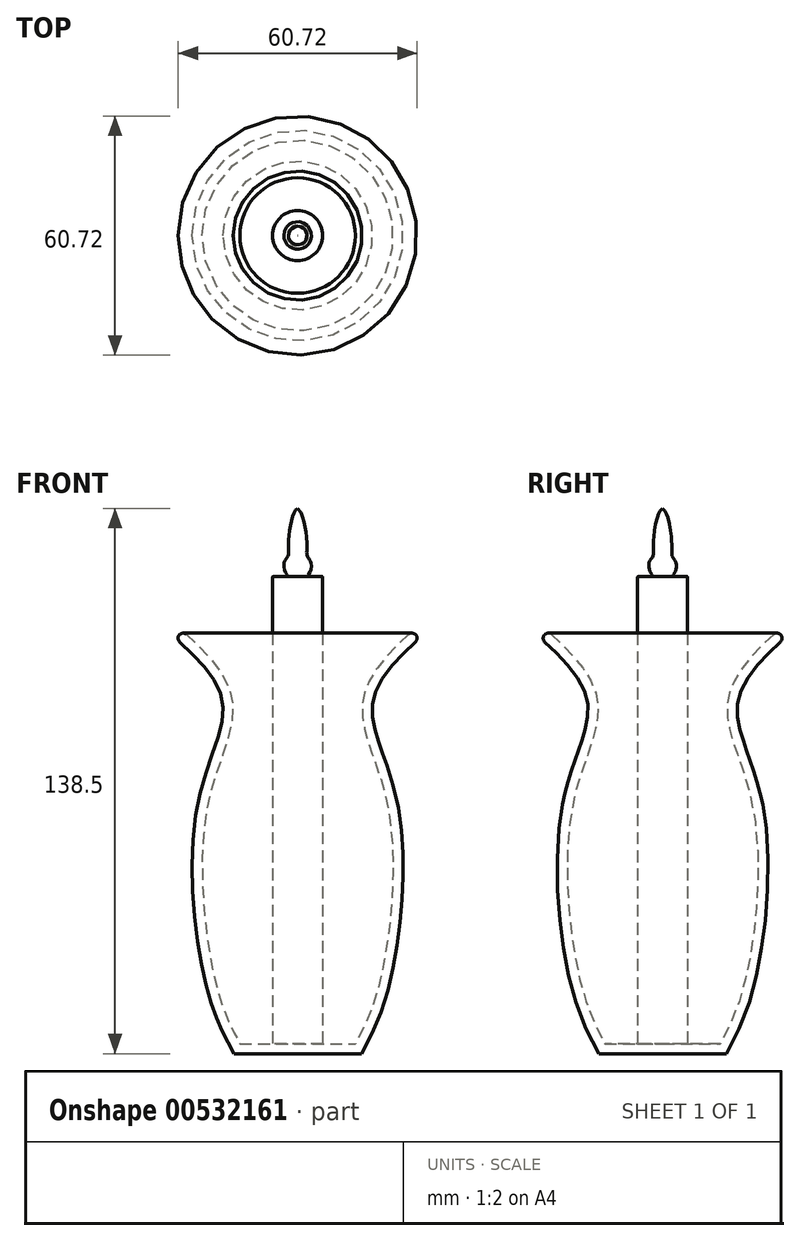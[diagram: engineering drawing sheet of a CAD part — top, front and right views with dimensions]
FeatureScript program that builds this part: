
annotation { "Feature Type Name" : "Feature", "Feature Type Description" : "" }
export const myFeature = defineFeature(function(context is Context, id is Id, definition is map)
    precondition{}
    {
        {
            var Q0;
            Q0=qCreatedBy(makeId("Front.planeOp"),FACE);
            var sketch = newSketch(context, id + "F0", { "sketchPlane" : qUnion([Q0])});
            skLineSegment(sketch, "E0", {"start": v(0, 51.45) * mm, "end": v(-32.36, 51.45) * mm});
            skPoint(sketch, "E1.4.internal.snap0", {"position": v(-16.18, 51.45) * mm});
            skFitSpline(sketch, "E1", {"points": [v(-32.36, 51.45) * mm, v(-19.09, 34.02) * mm, v(-25.3, 8.5) * mm, v(-23.03, -39) * mm, v(-16.18, -55.4) * mm], "startDerivative": vector(82.3, -74.73) * mm, "endDerivative": vector(36.18, -66.1) * mm});
            skLineSegment(sketch, "E2", {"start": v(-16.18, -55.4) * mm, "end": v(0, -55.4) * mm});
            skLineSegment(sketch, "E3", {"start": v(0, -55.4) * mm, "end": v(0, 51.45) * mm});
            skSolve(sketch);
        }
        {
            var Q0;
            Q0=makeQuery(id+"F0.imprint","IMPRINT",FACE,{"disambiguationData":[TD([[makeQuery(id+"F0.imprint","IMPRINT",EDGE,{"derivedFrom":sQuery(id+"F0.wireOp",EDGE,"E0")}),1.0]])]});
            var Q1;
            Q1=sQuery(id+"F0.wireOp",EDGE,"E3");
            revolve(context, id + "F1", {"entities" : qUnion([Q0]), "axis" : qUnion([Q1]), "revolveType" : RevolveType.FULL});
        }
        {
            var Q0;
            Q0=makeQuery(id+"F1.opRevolve","SWEPT_FACE",FACE,{"disambiguationData":[OSD([sQuery(id+"F0.wireOp",EDGE,"E0")])]});
            shell(context, id + "F2", {"entities" : qUnion([Q0]), "thickness" : 2.54 * mm});
        }
        {
            var Q0;
            Q0=makeQuery(id+"F2.opShell","OFFSET_FACE",FACE,{"disambiguationData":[OSD([sQuery(id+"F0.wireOp",EDGE,"E2")])]});
            var sketch = newSketch(context, id + "F3", { "sketchPlane" : qUnion([Q0])});
            skCircle(sketch, "E4", {"center": v(0, 0) * mm, "radius": 6.35 * mm});
            skSolve(sketch);
        }
        {
            var Q0;
            Q0 = qSketchRegion(id + "F3", true);
            extrude(context, id + "F4", {"entities" : qUnion([Q0]), "operationType" : NewBodyOperationType.ADD, "depth" : 118.76 * mm, "offsetDistance" : 25.4 * mm});
        }
        {
            var Q0;
            Q0=qCreatedBy(makeId("Front.planeOp"),FACE);
            var sketch = newSketch(context, id + "F5", { "sketchPlane" : qUnion([Q0])});
            skFitSpline(sketch, "E5", {"points": [v(0, 83.11) * mm, v(-2.34, 73.84) * mm, v(-2.5, 70.87) * mm, v(-3.47, 69.15) * mm, v(-2.29, 65.9) * mm, v(0, 65.92) * mm], "startDerivative": vector(-14.49, -6.91) * mm, "endDerivative": vector(13.28, 4.08) * mm});
            skLineSegment(sketch, "E6", {"start": v(0, 83.11) * mm, "end": v(0, 65.92) * mm});
            skSolve(sketch);
        }
        {
            var Q0;
            Q0=makeQuery(id+"F5.imprint","IMPRINT",FACE,{"disambiguationData":[TD([[makeQuery(id+"F5.imprint","IMPRINT",EDGE,{"derivedFrom":sQuery(id+"F5.wireOp",EDGE,"E5")}),1.0]])]});
            var Q1;
            Q1=sQuery(id+"F5.wireOp",EDGE,"E6");
            revolve(context, id + "F6", {"operationType" : NewBodyOperationType.ADD, "entities" : qUnion([Q0]), "axis" : qUnion([Q1]), "revolveType" : RevolveType.FULL});
        }
        {
            var Q0;
            {var subQ0=sQuery(id+"F3.wireOp",EDGE,"E4");Q0=makeQuery(id+"F6.boolean.opBoolean","SPLIT",FACE,{"disambiguationData":[TD([makeQuery(id+"F4.opExtrude","SWEPT_FACE",FACE,{"disambiguationData":[OSD([subQ0])]}),makeQuery(id+"F6.opRevolve","SWEPT_FACE",FACE,{"disambiguationData":[OSD([sQuery(id+"F5.wireOp",EDGE,"E5")])]})])],"derivedFrom":makeQuery(id+"F4.opExtrude","CAP_FACE",FACE,{"disambiguationData":[OSD([subQ0])],"isStart":false})});}
            fillet(context, id + "F7", {"entities" : qUnion([Q0]), "radius" : 0.25 * mm, "tangentPropagation" : true, "allowEdgeOverflow" : false});
        }
        {
            var Q0;
            Q0=makeQuery(id+"F1.opRevolve","SWEPT_FACE",FACE,{"disambiguationData":[OSD([sQuery(id+"F0.wireOp",EDGE,"E0")])]});
            fillet(context, id + "F8", {"entities" : qUnion([Q0]), "radius" : 1.27 * mm, "tangentPropagation" : true, "allowEdgeOverflow" : false});
        }
    });
